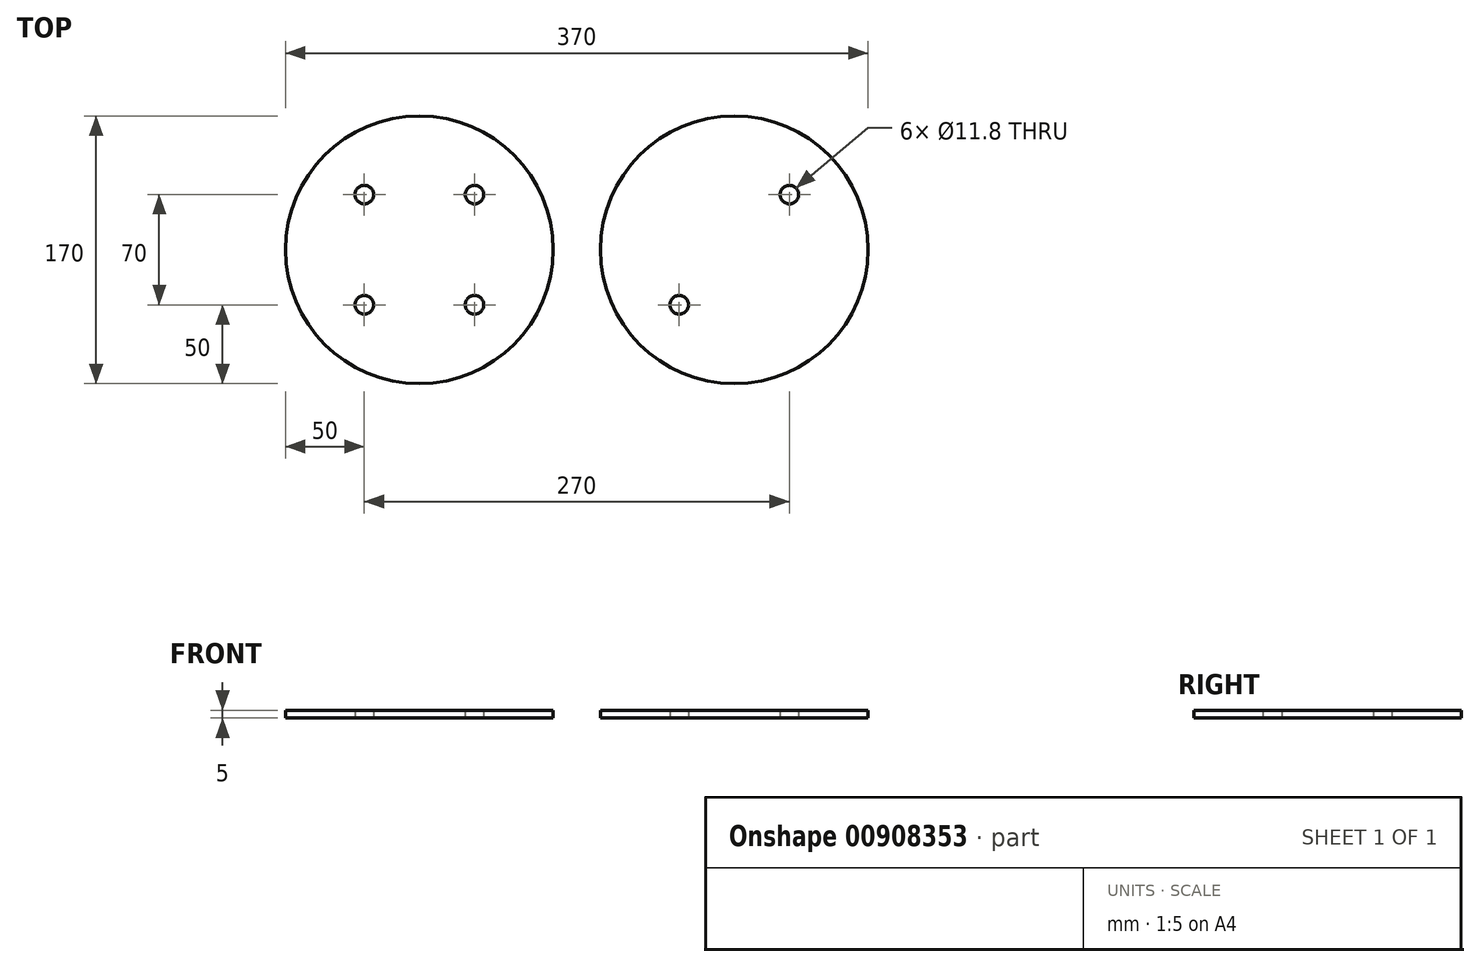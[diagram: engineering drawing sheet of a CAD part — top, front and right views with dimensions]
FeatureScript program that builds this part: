
annotation { "Feature Type Name" : "Feature", "Feature Type Description" : "" }
export const myFeature = defineFeature(function(context is Context, id is Id, definition is map)
    precondition{}
    {
        {
            var Q0;
            Q0=qCreatedBy(makeId("Top.planeOp"),FACE);
            var sketch = newSketch(context, id + "F0", { "sketchPlane" : qUnion([Q0])});
            skCircle(sketch, "E0", {"center": v(0, 0) * mm, "radius": 85 * mm});
            skLineSegment(sketch, "E1.bottom", {"start": v(-35, 35) * mm, "end": v(35, 35) * mm, "construction": true});
            skLineSegment(sketch, "E1.top", {"start": v(-35, -35) * mm, "end": v(35, -35) * mm, "construction": true});
            skLineSegment(sketch, "E1.left", {"start": v(-35, 35) * mm, "end": v(-35, -35) * mm, "construction": true});
            skLineSegment(sketch, "E1.right", {"start": v(35, 35) * mm, "end": v(35, -35) * mm, "construction": true});
            skCircle(sketch, "E2", {"center": v(-35, -35) * mm, "radius": 5.9 * mm});
            skCircle(sketch, "E3", {"center": v(35, -35) * mm, "radius": 5.9 * mm});
            skCircle(sketch, "E4", {"center": v(35, 35) * mm, "radius": 5.9 * mm});
            skCircle(sketch, "E5", {"center": v(-35, 35) * mm, "radius": 5.9 * mm});
            skCircle(sketch, "E6", {"center": v(200, 0) * mm, "radius": 85 * mm});
            skLineSegment(sketch, "E7.bottom", {"start": v(165, 35) * mm, "end": v(235, 35) * mm, "construction": true});
            skLineSegment(sketch, "E7.top", {"start": v(165, -35) * mm, "end": v(235, -35) * mm, "construction": true});
            skLineSegment(sketch, "E7.left", {"start": v(165, 35) * mm, "end": v(165, -35) * mm, "construction": true});
            skLineSegment(sketch, "E7.right", {"start": v(235, 35) * mm, "end": v(235, -35) * mm, "construction": true});
            skCircle(sketch, "E8", {"center": v(165, -35) * mm, "radius": 5.9 * mm});
            skCircle(sketch, "E9", {"center": v(235, 35) * mm, "radius": 5.9 * mm});
            skSolve(sketch);
        }
        {
            var Q0;
            Q0 = qSketchRegion(id + "F0", true);
            var Q1;
            Q1=makeQuery(id+"F0.imprint","IMPRINT",FACE,{"disambiguationData":[TD([[makeQuery(id+"F0.imprint","IMPRINT",EDGE,{"derivedFrom":sQuery(id+"F0.wireOp",EDGE,"E0")}),1.0]])]});
            extrude(context, id + "F1", {"entities" : qUnion([Q0, Q1]), "depth" : 5 * mm, "offsetDistance" : 25 * mm});
        }
    });
